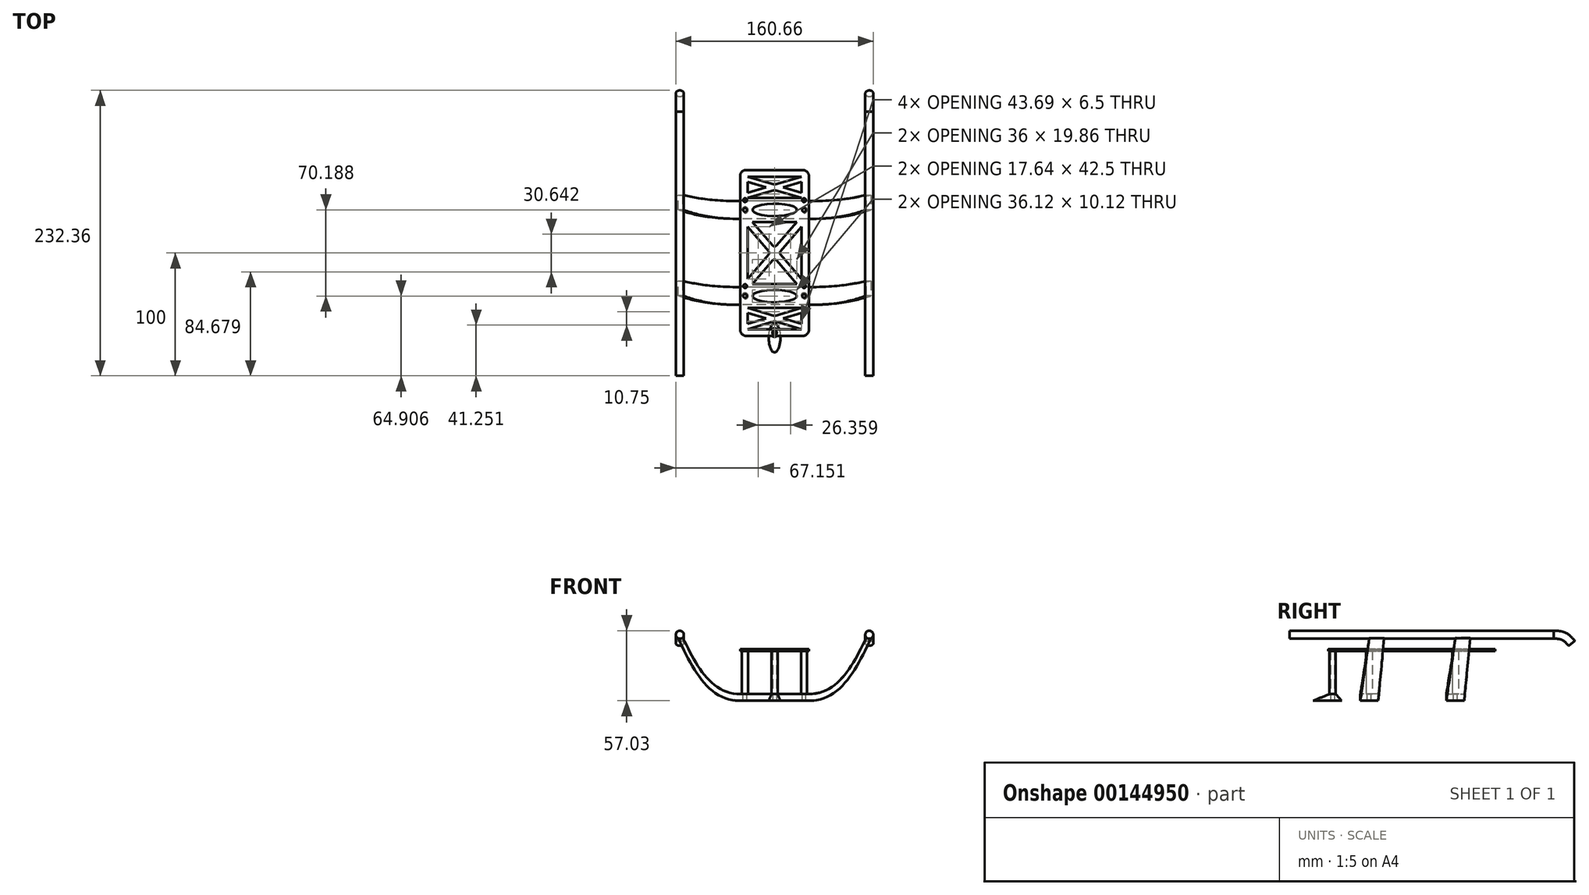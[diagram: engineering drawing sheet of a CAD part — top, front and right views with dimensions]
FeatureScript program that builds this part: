
annotation { "Feature Type Name" : "Feature", "Feature Type Description" : "" }
export const myFeature = defineFeature(function(context is Context, id is Id, definition is map)
    precondition{}
    {
        {
            var Q0;
            Q0=qCreatedBy(makeId("Top.planeOp"),FACE);
            var sketch = newSketch(context, id + "F0", { "sketchPlane" : qUnion([Q0])});
            skCircle(sketch, "E0", {"center": v(24, 35) * mm, "radius": 1.55 * mm});
            skCircle(sketch, "E1.MirrorC", {"center": v(-24, 35) * mm, "radius": 1.55 * mm});
            skCircle(sketch, "E2.MirrorC", {"center": v(-24, -35) * mm, "radius": 1.55 * mm});
            skCircle(sketch, "E3.MirrorC", {"center": v(24, -35) * mm, "radius": 1.55 * mm});
            skLineSegment(sketch, "E4.bottom", {"start": v(27.5, 27.75) * mm, "end": v(-27.5, 27.75) * mm});
            skLineSegment(sketch, "E4.top", {"start": v(27.5, 42.25) * mm, "end": v(-27.5, 42.25) * mm});
            skLineSegment(sketch, "E4.left", {"start": v(27.5, 27.75) * mm, "end": v(27.5, 42.25) * mm});
            skLineSegment(sketch, "E4.right", {"start": v(-27.5, 27.75) * mm, "end": v(-27.5, 42.25) * mm});
            skPoint(sketch, "E4.middle", {"position": v(0, 35) * mm});
            skPoint(sketch, "E5.MirrorP", {"position": v(0, -35) * mm});
            skLineSegment(sketch, "E6.MirrorCS", {"start": v(-27.5, -27.75) * mm, "end": v(-27.5, -42.25) * mm});
            skLineSegment(sketch, "E7.MirrorCS", {"start": v(27.5, -27.75) * mm, "end": v(27.5, -42.25) * mm});
            skLineSegment(sketch, "E8.MirrorCS", {"start": v(27.5, -27.75) * mm, "end": v(-27.5, -27.75) * mm});
            skLineSegment(sketch, "E9.MirrorCS", {"start": v(27.5, -42.25) * mm, "end": v(-27.5, -42.25) * mm});
            skSolve(sketch);
        }
        {
            var Q0;
            Q0 = qSketchRegion(id + "F0", true);
            extrude(context, id + "F1", {"entities" : qUnion([Q0]), "oppositeDirection" : true, "depth" : 5.5 * mm});
        }
        {
            var Q0;
            Q0=makeQuery(id+"F1.opExtrude","CAP_FACE",FACE,{"disambiguationData":[OSD([sQuery(id+"F0.wireOp",EDGE,"E0"),sQuery(id+"F0.wireOp",EDGE,"E1.MirrorC"),sQuery(id+"F0.wireOp",EDGE,"E4.bottom"),sQuery(id+"F0.wireOp",EDGE,"E4.top"),sQuery(id+"F0.wireOp",EDGE,"E4.left"),sQuery(id+"F0.wireOp",EDGE,"E4.right")])],"isStart":true});
            cPlane(context, id + "F2", {"entities" : qUnion([Q0]), "cplaneType" : CPlaneType.OFFSET, "offset" : 47 * mm, "width" : 150 * mm, "height" : 150 * mm});
        }
        {
            var Q0;
            Q0=qCreatedBy(id+"F2.planeOp",FACE);
            var sketch = newSketch(context, id + "F3", { "sketchPlane" : qUnion([Q0])});
            skLineSegment(sketch, "E10.bottom", {"start": v(-79, 47.25) * mm, "end": v(-75, 47.25) * mm});
            skLineSegment(sketch, "E10.top", {"start": v(-79, 35.25) * mm, "end": v(-75, 35.25) * mm});
            skLineSegment(sketch, "E10.left", {"start": v(-79, 47.25) * mm, "end": v(-79, 35.25) * mm});
            skLineSegment(sketch, "E10.right", {"start": v(-75, 47.25) * mm, "end": v(-75, 35.25) * mm});
            skLineSegment(sketch, "E11.bottom", {"start": v(-79, -22.75) * mm, "end": v(-75, -22.75) * mm});
            skLineSegment(sketch, "E11.top", {"start": v(-79, -34.75) * mm, "end": v(-75, -34.75) * mm});
            skLineSegment(sketch, "E11.left", {"start": v(-79, -22.75) * mm, "end": v(-79, -34.75) * mm});
            skLineSegment(sketch, "E11.right", {"start": v(-75, -22.75) * mm, "end": v(-75, -34.75) * mm});
            skLineSegment(sketch, "E12.MirrorCS", {"start": v(79, 47.25) * mm, "end": v(75, 47.25) * mm});
            skLineSegment(sketch, "E13.MirrorCS", {"start": v(79, 35.25) * mm, "end": v(75, 35.25) * mm});
            skLineSegment(sketch, "E14.MirrorCS", {"start": v(79, 47.25) * mm, "end": v(79, 35.25) * mm});
            skLineSegment(sketch, "E15.MirrorCS", {"start": v(75, 47.25) * mm, "end": v(75, 35.25) * mm});
            skLineSegment(sketch, "E16.MirrorCS", {"start": v(79, -22.75) * mm, "end": v(75, -22.75) * mm});
            skLineSegment(sketch, "E17.MirrorCS", {"start": v(79, -34.75) * mm, "end": v(75, -34.75) * mm});
            skLineSegment(sketch, "E18.MirrorCS", {"start": v(75, -22.75) * mm, "end": v(75, -34.75) * mm});
            skLineSegment(sketch, "E19.MirrorCS", {"start": v(79, -22.75) * mm, "end": v(79, -34.75) * mm});
            skSolve(sketch);
        }
        {
            var Q0;
            Q0 = qSketchRegion(id + "F3", true);
            extrude(context, id + "F4", {"entities" : qUnion([Q0]), "depth" : 1 * mm, "symmetric" : true});
        }
        {
            var Q0;
            Q0=makeQuery(id+"F1.opExtrude","SWEPT_FACE",FACE,{"disambiguationData":[OSD([sQuery(id+"F0.wireOp",EDGE,"E4.right")])]});
            var Q1;
            Q1=makeQuery(id+"F4.opExtrude","CAP_FACE",FACE,{"disambiguationData":[OSD([sQuery(id+"F3.wireOp",EDGE,"E10.bottom"),sQuery(id+"F3.wireOp",EDGE,"E10.top"),sQuery(id+"F3.wireOp",EDGE,"E10.left"),sQuery(id+"F3.wireOp",EDGE,"E10.right")])],"isStart":true});
            loft(context, id + "F5", {"operationType" : NewBodyOperationType.ADD, "startCondition" : LoftEndDerivativeType.NORMAL_TO_PROFILE, "startMagnitude" : 1.5, "sheetProfilesArray" : [{ "sheetProfileEntities" : qUnion([Q0]) }, { "sheetProfileEntities" : qUnion([Q1]) }]});
        }
        {
            var Q0;
            Q0=makeQuery(id+"F1.opExtrude","SWEPT_FACE",FACE,{"disambiguationData":[OSD([sQuery(id+"F0.wireOp",EDGE,"E6.MirrorCS")])]});
            var Q1;
            Q1=makeQuery(id+"F4.opExtrude","CAP_FACE",FACE,{"disambiguationData":[OSD([sQuery(id+"F3.wireOp",EDGE,"E11.bottom"),sQuery(id+"F3.wireOp",EDGE,"E11.top"),sQuery(id+"F3.wireOp",EDGE,"E11.left"),sQuery(id+"F3.wireOp",EDGE,"E11.right")])],"isStart":true});
            loft(context, id + "F6", {"operationType" : NewBodyOperationType.ADD, "startCondition" : LoftEndDerivativeType.NORMAL_TO_PROFILE, "startMagnitude" : 1.5, "sheetProfilesArray" : [{ "sheetProfileEntities" : qUnion([Q0]) }, { "sheetProfileEntities" : qUnion([Q1]) }]});
        }
        {
            var Q0;
            Q0=makeQuery(id+"F1.opExtrude","SWEPT_FACE",FACE,{"disambiguationData":[OSD([sQuery(id+"F0.wireOp",EDGE,"E7.MirrorCS")])]});
            var Q1;
            Q1=makeQuery(id+"F4.opExtrude","CAP_FACE",FACE,{"disambiguationData":[OSD([sQuery(id+"F3.wireOp",EDGE,"E16.MirrorCS"),sQuery(id+"F3.wireOp",EDGE,"E17.MirrorCS"),sQuery(id+"F3.wireOp",EDGE,"E18.MirrorCS"),sQuery(id+"F3.wireOp",EDGE,"E19.MirrorCS")])],"isStart":true});
            loft(context, id + "F7", {"operationType" : NewBodyOperationType.ADD, "startCondition" : LoftEndDerivativeType.NORMAL_TO_PROFILE, "startMagnitude" : 1.5, "sheetProfilesArray" : [{ "sheetProfileEntities" : qUnion([Q0]) }, { "sheetProfileEntities" : qUnion([Q1]) }]});
        }
        {
            var Q0;
            Q0=makeQuery(id+"F1.opExtrude","SWEPT_FACE",FACE,{"disambiguationData":[OSD([sQuery(id+"F0.wireOp",EDGE,"E4.left")])]});
            var Q1;
            Q1=makeQuery(id+"F4.opExtrude","CAP_FACE",FACE,{"disambiguationData":[OSD([sQuery(id+"F3.wireOp",EDGE,"E12.MirrorCS"),sQuery(id+"F3.wireOp",EDGE,"E13.MirrorCS"),sQuery(id+"F3.wireOp",EDGE,"E14.MirrorCS"),sQuery(id+"F3.wireOp",EDGE,"E15.MirrorCS")])],"isStart":true});
            loft(context, id + "F8", {"operationType" : NewBodyOperationType.ADD, "startCondition" : LoftEndDerivativeType.NORMAL_TO_PROFILE, "startMagnitude" : 1.5, "sheetProfilesArray" : [{ "sheetProfileEntities" : qUnion([Q0]) }, { "sheetProfileEntities" : qUnion([Q1]) }]});
        }
        {
            var Q0;
            Q0=qCreatedBy(makeId("Front.planeOp"),FACE);
            var sketch = newSketch(context, id + "F9", { "sketchPlane" : qUnion([Q0])});
            skCircle(sketch, "E20", {"center": v(-77.08, 48.25) * mm, "radius": 3.25 * mm});
            skCircle(sketch, "E21.MirrorC", {"center": v(77.08, 48.25) * mm, "radius": 3.25 * mm});
            skSolve(sketch);
        }
        {
            var Q0;
            Q0 = qSketchRegion(id + "F9", true);
            extrude(context, id + "F10", {"entities" : qUnion([Q0]), "operationType" : NewBodyOperationType.ADD, "depth" : 100 * mm, "hasSecondDirection" : true, "secondDirectionOppositeDirection" : true, "secondDirectionDepth" : 115 * mm});
        }
        {
            var Q0;
            Q0=qCreatedBy(makeId("Right.planeOp"),FACE);
            var sketch = newSketch(context, id + "F11", { "sketchPlane" : qUnion([Q0])});
            skFitSpline(sketch, "E22", {"points": [v(115, 54.9) * mm, v(123.56, 53.94) * mm, v(128.8, 51.44) * mm, v(135, 45.49) * mm], "startDerivative": vector(20.16, 0.9) * mm, "endDerivative": vector(29.36, -33.3) * mm});
            skPoint(sketch, "E23", {"position": v(115, 57.99) * mm});
            skSolve(sketch);
        }
        {
            var Q0;
            Q0=makeQuery(id+"F10.opExtrude","CAP_FACE",FACE,{"disambiguationData":[OSD([sQuery(id+"F9.wireOp",EDGE,"E20")])],"isStart":true});
            var Q1;
            Q1=makeQuery(id+"F10.opExtrude","CAP_FACE",FACE,{"disambiguationData":[OSD([sQuery(id+"F9.wireOp",EDGE,"E21.MirrorC")])],"isStart":true});
            var Q2;
            Q2=sQuery(id+"F11.wireOp",EDGE,"E22");
            sweep(context, id + "F12", {"operationType" : NewBodyOperationType.ADD, "profiles" : qUnion([Q0, Q1]), "path" : qUnion([Q2])});
        }
        {
            var Q0;
            Q0=makeQuery(id+"F1.opExtrude","CAP_FACE",FACE,{"disambiguationData":[OSD([sQuery(id+"F0.wireOp",EDGE,"E0"),sQuery(id+"F0.wireOp",EDGE,"E1.MirrorC"),sQuery(id+"F0.wireOp",EDGE,"E4.bottom"),sQuery(id+"F0.wireOp",EDGE,"E4.top"),sQuery(id+"F0.wireOp",EDGE,"E4.left"),sQuery(id+"F0.wireOp",EDGE,"E4.right")])],"isStart":true});
            cPlane(context, id + "F13", {"entities" : qUnion([Q0]), "cplaneType" : CPlaneType.OFFSET, "offset" : 35 * mm, "width" : 150 * mm, "height" : 150 * mm});
        }
        {
            var Q0;
            Q0=qCreatedBy(id+"F13.planeOp",FACE);
            var sketch = newSketch(context, id + "F14", { "sketchPlane" : qUnion([Q0])});
            skLineSegment(sketch, "E24.bottom", {"start": v(23, -67.5) * mm, "end": v(2.55, -67.5) * mm});
            skLineSegment(sketch, "E24.top", {"start": v(23, 67.5) * mm, "end": v(-23, 67.5) * mm});
            skLineSegment(sketch, "E24.left", {"start": v(28, -62.5) * mm, "end": v(28, 62.5) * mm});
            skLineSegment(sketch, "E24.right", {"start": v(-28, -62.5) * mm, "end": v(-28, 62.5) * mm});
            skLineSegment(sketch, "E25", {"start": v(21.85, -57.83) * mm, "end": v(21.85, -48.92) * mm});
            skLineSegment(sketch, "E26", {"start": v(21.85, -48.92) * mm, "end": v(6.88, -53.37) * mm});
            skLineSegment(sketch, "E27", {"start": v(6.88, -53.37) * mm, "end": v(21.85, -57.83) * mm});
            skLineSegment(sketch, "E28.MirrorCS", {"start": v(-6.88, -53.37) * mm, "end": v(-21.85, -57.83) * mm});
            skLineSegment(sketch, "E29.MirrorCS", {"start": v(-21.85, -57.83) * mm, "end": v(-21.85, -48.92) * mm});
            skLineSegment(sketch, "E30.MirrorCS", {"start": v(-21.85, -48.92) * mm, "end": v(-6.88, -53.37) * mm});
            skLineSegment(sketch, "E31", {"start": v(21.85, -62) * mm, "end": v(2.42, -62) * mm});
            skLineSegment(sketch, "E32", {"start": v(-21.85, -62) * mm, "end": v(0, -55.5) * mm});
            skLineSegment(sketch, "E33", {"start": v(0, -55.5) * mm, "end": v(21.85, -62) * mm});
            skLineSegment(sketch, "E34", {"start": v(2.98, -53.37) * mm, "end": v(-2.47, -53.37) * mm});
            skLineSegment(sketch, "E35.MirrorCS", {"start": v(0, -51.25) * mm, "end": v(21.85, -44.75) * mm});
            skLineSegment(sketch, "E36.MirrorCS", {"start": v(21.85, -44.75) * mm, "end": v(-21.85, -44.75) * mm});
            skLineSegment(sketch, "E37.MirrorCS", {"start": v(-21.85, -44.75) * mm, "end": v(0, -51.25) * mm});
            skLineSegment(sketch, "E38.MirrorCS", {"start": v(2.98, 53.37) * mm, "end": v(-2.47, 53.37) * mm});
            skLineSegment(sketch, "E39.MirrorCS", {"start": v(-21.85, 62) * mm, "end": v(0, 55.5) * mm});
            skLineSegment(sketch, "E40.MirrorCS", {"start": v(0, 55.5) * mm, "end": v(21.85, 62) * mm});
            skLineSegment(sketch, "E41.MirrorCS", {"start": v(6.88, 53.37) * mm, "end": v(21.85, 57.83) * mm});
            skLineSegment(sketch, "E42.MirrorCS", {"start": v(21.85, 57.83) * mm, "end": v(21.85, 48.92) * mm});
            skLineSegment(sketch, "E43.MirrorCS", {"start": v(21.85, 48.92) * mm, "end": v(6.88, 53.37) * mm});
            skLineSegment(sketch, "E44.MirrorCS", {"start": v(-21.85, 44.75) * mm, "end": v(0, 51.25) * mm});
            skLineSegment(sketch, "E45.MirrorCS", {"start": v(21.85, 62) * mm, "end": v(-21.85, 62) * mm});
            skLineSegment(sketch, "E46.MirrorCS", {"start": v(-21.85, 48.92) * mm, "end": v(-6.88, 53.37) * mm});
            skLineSegment(sketch, "E47.MirrorCS", {"start": v(-21.85, 57.83) * mm, "end": v(-21.85, 48.92) * mm});
            skLineSegment(sketch, "E48.MirrorCS", {"start": v(-6.88, 53.37) * mm, "end": v(-21.85, 57.83) * mm});
            skLineSegment(sketch, "E49.MirrorCS", {"start": v(21.85, 44.75) * mm, "end": v(-21.85, 44.75) * mm});
            skLineSegment(sketch, "E50.MirrorCS", {"start": v(0, 51.25) * mm, "end": v(21.85, 44.75) * mm});
            skEllipse(sketch, "E51", {"center": v(0, 35.1) * mm, "majorRadius": 18.06 * mm, "minorRadius": 5.06 * mm, "majorAxis": v(1, 0)});
            skEllipse(sketch, "E52.MirrorC", {"center": v(0, -35.1) * mm, "majorRadius": 18.06 * mm, "minorRadius": 5.06 * mm, "majorAxis": v(1, 0)});
            skPoint(sketch, "E53.visualSharp", {"position": v(-28, 67.5) * mm});
            skArc(sketch, "E53.filletArc", {"start": v(-23, 67.5) * mm, "mid": v(-26.54, 66.04) * mm, "end": v(-28, 62.5) * mm});
            skPoint(sketch, "E54.visualSharp", {"position": v(28, 67.5) * mm});
            skArc(sketch, "E54.filletArc", {"start": v(28, 62.5) * mm, "mid": v(26.54, 66.04) * mm, "end": v(23, 67.5) * mm});
            skPoint(sketch, "E55.visualSharp", {"position": v(28, -67.5) * mm});
            skArc(sketch, "E55.filletArc", {"start": v(23, -67.5) * mm, "mid": v(26.54, -66.04) * mm, "end": v(28, -62.5) * mm});
            skPoint(sketch, "E56.visualSharp", {"position": v(-28, -67.5) * mm});
            skArc(sketch, "E56.filletArc", {"start": v(-28, -62.5) * mm, "mid": v(-26.54, -66.04) * mm, "end": v(-23, -67.5) * mm});
            skArc(sketch, "E57", {"start": v(-1.98, -67.68) * mm, "mid": v(0, -68.3) * mm, "end": v(1.98, -67.68) * mm});
            skArc(sketch, "E58.trimOffspring", {"start": v(1.88, -61.84) * mm, "mid": v(0, -61.3) * mm, "end": v(-1.88, -61.84) * mm});
            skLineSegment(sketch, "E59.trimOffspring", {"start": v(-2.42, -62) * mm, "end": v(-21.85, -62) * mm});
            skLineSegment(sketch, "E60.trimOffspring", {"start": v(-2.55, -67.5) * mm, "end": v(-23, -67.5) * mm});
            skPoint(sketch, "E61.visualSharp", {"position": v(2.22, -67.5) * mm});
            skArc(sketch, "E61.filletArc", {"start": v(2.55, -67.5) * mm, "mid": v(2.25, -67.55) * mm, "end": v(1.98, -67.68) * mm});
            skPoint(sketch, "E62.visualSharp", {"position": v(2.1, -62) * mm});
            skArc(sketch, "E62.filletArc", {"start": v(1.88, -61.84) * mm, "mid": v(2.14, -61.96) * mm, "end": v(2.42, -62) * mm});
            skPoint(sketch, "E63.visualSharp", {"position": v(-2.1, -62) * mm});
            skArc(sketch, "E63.filletArc", {"start": v(-2.42, -62) * mm, "mid": v(-2.14, -61.96) * mm, "end": v(-1.88, -61.84) * mm});
            skPoint(sketch, "E64.visualSharp", {"position": v(-2.22, -67.5) * mm});
            skArc(sketch, "E64.filletArc", {"start": v(-1.98, -67.68) * mm, "mid": v(-2.25, -67.55) * mm, "end": v(-2.55, -67.5) * mm});
            skLineSegment(sketch, "E65.bottom", {"start": v(-18, 25.25) * mm, "end": v(18, 25.25) * mm});
            skLineSegment(sketch, "E65.top", {"start": v(-18, -25.25) * mm, "end": v(18, -25.25) * mm});
            skLineSegment(sketch, "E65.left", {"start": v(-22, 21.25) * mm, "end": v(-22, -21.25) * mm});
            skLineSegment(sketch, "E65.right", {"start": v(22, 21.25) * mm, "end": v(22, -21.25) * mm});
            skLineSegment(sketch, "E66", {"start": v(-18, 25.25) * mm, "end": v(-1.52, 6.09) * mm});
            skLineSegment(sketch, "E67", {"start": v(-22, 21.25) * mm, "end": v(-4.84, 1.3) * mm});
            skLineSegment(sketch, "E68", {"start": v(-22, -21.25) * mm, "end": v(-4.84, -1.3) * mm});
            skLineSegment(sketch, "E69", {"start": v(-18, -25.25) * mm, "end": v(-1.52, -6.09) * mm});
            skPoint(sketch, "E70.orphan", {"position": v(-22, 25.25) * mm});
            skPoint(sketch, "E71.orphan", {"position": v(22, 25.25) * mm});
            skPoint(sketch, "E72.orphan", {"position": v(22, -25.25) * mm});
            skPoint(sketch, "E73.orphan", {"position": v(-22, -25.25) * mm});
            skLineSegment(sketch, "E74.trimOffspring", {"start": v(1.52, -6.09) * mm, "end": v(18, -25.25) * mm});
            skLineSegment(sketch, "E75.trimOffspring", {"start": v(1.52, 6.09) * mm, "end": v(18, 25.25) * mm});
            skLineSegment(sketch, "E76.trimOffspring", {"start": v(4.84, -1.3) * mm, "end": v(22, -21.25) * mm});
            skLineSegment(sketch, "E77.trimOffspring", {"start": v(4.84, 1.3) * mm, "end": v(22, 21.25) * mm});
            skPoint(sketch, "E78.visualSharp", {"position": v(0, 4.33) * mm});
            skArc(sketch, "E78.filletArc", {"start": v(-1.52, 6.09) * mm, "mid": v(0, 5.4) * mm, "end": v(1.52, 6.09) * mm});
            skPoint(sketch, "E79.visualSharp", {"position": v(3.72, 0) * mm});
            skArc(sketch, "E79.filletArc", {"start": v(4.84, 1.3) * mm, "mid": v(4.36, 0) * mm, "end": v(4.84, -1.3) * mm});
            skPoint(sketch, "E80.visualSharp", {"position": v(0, -4.33) * mm});
            skArc(sketch, "E80.filletArc", {"start": v(1.52, -6.09) * mm, "mid": v(0, -5.4) * mm, "end": v(-1.52, -6.09) * mm});
            skPoint(sketch, "E81.visualSharp", {"position": v(-3.72, 0) * mm});
            skArc(sketch, "E81.filletArc", {"start": v(-4.84, -1.3) * mm, "mid": v(-4.36, 0) * mm, "end": v(-4.84, 1.3) * mm});
            skSolve(sketch);
        }
        {
            var Q0;
            Q0 = qSketchRegion(id + "F14", true);
            extrude(context, id + "F15", {"entities" : qUnion([Q0]), "depth" : 1.5 * mm});
        }
        {
            var Q0;
            Q0=makeQuery(id+"F0.imprint","IMPRINT",FACE,{"disambiguationData":[TD([[makeQuery(id+"F0.imprint","IMPRINT",EDGE,{"derivedFrom":sQuery(id+"F0.wireOp",EDGE,"E3.MirrorC")}),1.0]])]});
            var sketch = newSketch(context, id + "F16", { "sketchPlane" : qUnion([Q0])});
            skEllipse(sketch, "E82", {"center": v(0, -64.7) * mm, "majorRadius": 2.5 * mm, "minorRadius": 2.5 * mm, "majorAxis": v(0, 1)});
            skSolve(sketch);
        }
        {
            var Q0;
            Q0=makeQuery(id+"F1.opExtrude","CAP_FACE",FACE,{"disambiguationData":[OSD([sQuery(id+"F0.wireOp",EDGE,"E3.MirrorC"),sQuery(id+"F0.wireOp",EDGE,"E2.MirrorC"),sQuery(id+"F0.wireOp",EDGE,"E6.MirrorCS"),sQuery(id+"F0.wireOp",EDGE,"E7.MirrorCS"),sQuery(id+"F0.wireOp",EDGE,"E8.MirrorCS"),sQuery(id+"F0.wireOp",EDGE,"E9.MirrorCS")])],"isStart":false});
            var sketch = newSketch(context, id + "F17", { "sketchPlane" : qUnion([Q0])});
            skEllipse(sketch, "E83", {"center": v(0, 69.16) * mm, "majorRadius": 11.75 * mm, "minorRadius": 4.76 * mm, "majorAxis": v(0, -1)});
            skSolve(sketch);
        }
        {
            var Q1;
            Q1 = qSketchRegion(id + "F16", true);
            var Q2;
            Q2 = qSketchRegion(id + "F17", true);
            loft(context, id + "F18", {"sheetProfilesArray" : [{ "sheetProfileEntities" : qUnion([Q1]) }, { "sheetProfileEntities" : qUnion([Q2]) }]});
        }
        {
            var Q0;
            Q0=makeQuery(id+"F15.opExtrude","CAP_FACE",FACE,{"disambiguationData":[OSD([sQuery(id+"F14.wireOp",EDGE,"E24.bottom"),sQuery(id+"F14.wireOp",EDGE,"E24.top"),sQuery(id+"F14.wireOp",EDGE,"E24.left"),sQuery(id+"F14.wireOp",EDGE,"E24.right"),sQuery(id+"F14.wireOp",EDGE,"E25"),sQuery(id+"F14.wireOp",EDGE,"E26"),sQuery(id+"F14.wireOp",EDGE,"E27"),sQuery(id+"F14.wireOp",EDGE,"E28.MirrorCS"),sQuery(id+"F14.wireOp",EDGE,"E29.MirrorCS"),sQuery(id+"F14.wireOp",EDGE,"E30.MirrorCS"),sQuery(id+"F14.wireOp",EDGE,"E31"),sQuery(id+"F14.wireOp",EDGE,"E32"),sQuery(id+"F14.wireOp",EDGE,"E33"),sQuery(id+"F14.wireOp",EDGE,"E35.MirrorCS"),sQuery(id+"F14.wireOp",EDGE,"E36.MirrorCS"),sQuery(id+"F14.wireOp",EDGE,"E37.MirrorCS"),sQuery(id+"F14.wireOp",EDGE,"E39.MirrorCS"),sQuery(id+"F14.wireOp",EDGE,"E40.MirrorCS"),sQuery(id+"F14.wireOp",EDGE,"E41.MirrorCS"),sQuery(id+"F14.wireOp",EDGE,"E42.MirrorCS"),sQuery(id+"F14.wireOp",EDGE,"E43.MirrorCS"),sQuery(id+"F14.wireOp",EDGE,"E44.MirrorCS"),sQuery(id+"F14.wireOp",EDGE,"E45.MirrorCS"),sQuery(id+"F14.wireOp",EDGE,"E46.MirrorCS"),sQuery(id+"F14.wireOp",EDGE,"E47.MirrorCS"),sQuery(id+"F14.wireOp",EDGE,"E48.MirrorCS"),sQuery(id+"F14.wireOp",EDGE,"E49.MirrorCS"),sQuery(id+"F14.wireOp",EDGE,"E50.MirrorCS"),sQuery(id+"F14.wireOp",EDGE,"41cgnIPL-npWc-O3OT-IIvp-3opdmebJhPuE"),sQuery(id+"F14.wireOp",EDGE,"cnqzEcAR-puum-2v5H-bPeM-nhvkTepjbg7f"),sQuery(id+"F14.wireOp",EDGE,"ZUyBv95D-Vip0-E0xQ-HOKZ-qXVskTSMhhZ4"),sQuery(id+"F14.wireOp",EDGE,"QW4Knzpe-XfPx-6G3O-fQ7r-xCA8DHTI8llc"),sQuery(id+"F14.wireOp",EDGE,"u5ZCEIEt-8dGf-CeKo-rW56-BvbBlPJxl9Av"),sQuery(id+"F14.wireOp",EDGE,"tRerhao7-xNC6-3Qj8-PqBg-vBzmJME0fykC"),sQuery(id+"F14.wireOp",EDGE,"34f72953-b367-436d-b2e1-794d6ac8d1dc0.MirrorCS"),sQuery(id+"F14.wireOp",EDGE,"e1a0620d-9711-44c7-a052-cdfd6f5fabb40.MirrorCS"),sQuery(id+"F14.wireOp",EDGE,"f9968c47-6fa3-4d05-afce-87440d7f02980.MirrorCS"),sQuery(id+"F14.wireOp",EDGE,"cde4a5db-1fe4-4333-8411-bf7d7e01e0120.MirrorCS"),sQuery(id+"F14.wireOp",EDGE,"0ad4e2a6-e274-4dd3-8f10-cc4f6a0458050.MirrorCS"),sQuery(id+"F14.wireOp",EDGE,"46e521f6-c0f6-47cd-9bc7-52dcf3b3e5ab0.MirrorCS"),sQuery(id+"F14.wireOp",EDGE,"E51"),sQuery(id+"F14.wireOp",EDGE,"E52.MirrorC"),sQuery(id+"F14.wireOp",EDGE,"E53.filletArc"),sQuery(id+"F14.wireOp",EDGE,"E54.filletArc"),sQuery(id+"F14.wireOp",EDGE,"E55.filletArc"),sQuery(id+"F14.wireOp",EDGE,"E56.filletArc")])],"isStart":true});
            var sketch = newSketch(context, id + "F19", { "sketchPlane" : qUnion([Q0])});
            skCircle(sketch, "E84", {"center": v(0, 64.95) * mm, "radius": 2.5 * mm});
            skSolve(sketch);
        }
        {
            var Q0;
            Q0 = qSketchRegion(id + "F19", true);
            var Q1;
            Q1=makeQuery(id+"F18.opLoft","CAP_FACE",FACE,{"disambiguationData":[OSD([makeQuery(id+"F16.imprint","IMPRINT",FACE,{"disambiguationData":[TD([[makeQuery(id+"F16.imprint","IMPRINT",EDGE,{"derivedFrom":sQuery(id+"F16.wireOp",EDGE,"E82")}),1.0]])]})])],"isStart":true});
            extrude(context, id + "F20", {"entities" : qUnion([Q0]), "endBound" : BoundingType.UP_TO_SURFACE, "endBoundEntityFace" : qUnion([Q1]), "depth" : 25 * mm});
        }
        {
            var Q0;
            Q0=makeQuery(id+"F18.opLoft","CAP_FACE",FACE,{"disambiguationData":[OSD([makeQuery(id+"F17.imprint","IMPRINT",FACE,{"disambiguationData":[TD([[makeQuery(id+"F17.imprint","IMPRINT",EDGE,{"derivedFrom":sQuery(id+"F17.wireOp",EDGE,"E83")}),1.0]])]})])],"isStart":true});
            var sketch = newSketch(context, id + "F21", { "sketchPlane" : qUnion([Q0])});
            skCircle(sketch, "E85", {"center": v(0, 64.95) * mm, "radius": 1.65 * mm});
            skSolve(sketch);
        }
        {
            var Q0;
            Q0 = qSketchRegion(id + "F21", true);
            extrude(context, id + "F22", {"entities" : qUnion([Q0]), "operationType" : NewBodyOperationType.REMOVE, "endBound" : BoundingType.THROUGH_ALL, "oppositeDirection" : true, "depth" : 25 * mm});
        }
        {
            var Q0;
            Q0=makeQuery(id+"F15.opExtrude","CAP_FACE",FACE,{"disambiguationData":[OSD([sQuery(id+"F14.wireOp",EDGE,"E24.bottom"),sQuery(id+"F14.wireOp",EDGE,"E24.top"),sQuery(id+"F14.wireOp",EDGE,"E24.left"),sQuery(id+"F14.wireOp",EDGE,"E24.right")])],"isStart":false});
            var sketch = newSketch(context, id + "F23", { "sketchPlane" : qUnion([Q0])});
            skCircle(sketch, "E86", {"center": v(-24, 35) * mm, "radius": 1.55 * mm});
            skCircle(sketch, "E87", {"center": v(24, 35) * mm, "radius": 1.55 * mm});
            skCircle(sketch, "E88", {"center": v(-24, -35) * mm, "radius": 1.55 * mm});
            skCircle(sketch, "E89", {"center": v(24, -35) * mm, "radius": 1.55 * mm});
            skCircle(sketch, "E90", {"center": v(-24, -27) * mm, "radius": 1.55 * mm});
            skCircle(sketch, "E91", {"center": v(-24, 43) * mm, "radius": 1.55 * mm});
            skCircle(sketch, "E92.MirrorC", {"center": v(24, 43) * mm, "radius": 1.55 * mm});
            skCircle(sketch, "E93.MirrorC", {"center": v(24, -27) * mm, "radius": 1.55 * mm});
            skSolve(sketch);
        }
        {
            var Q0;
            Q0 = qSketchRegion(id + "F23", true);
            var Q1;
            Q1=makeQuery(id+"F15.opExtrude","CAP_FACE",FACE,{"disambiguationData":[OSD([sQuery(id+"F14.wireOp",EDGE,"E24.bottom"),sQuery(id+"F14.wireOp",EDGE,"E24.top"),sQuery(id+"F14.wireOp",EDGE,"E24.left"),sQuery(id+"F14.wireOp",EDGE,"E24.right")])],"isStart":true});
            extrude(context, id + "F24", {"entities" : qUnion([Q0]), "operationType" : NewBodyOperationType.REMOVE, "endBound" : BoundingType.UP_TO_SURFACE, "oppositeDirection" : true, "endBoundEntityFace" : qUnion([Q1]), "depth" : 25 * mm});
        }
        {
            var Q0;
            Q0=makeQuery(id+"F0.imprint","IMPRINT",FACE,{"disambiguationData":[TD([[makeQuery(id+"F0.imprint","IMPRINT",EDGE,{"derivedFrom":sQuery(id+"F0.wireOp",EDGE,"E0")}),-1.0]])]});
            var sketch = newSketch(context, id + "F25", { "sketchPlane" : qUnion([Q0])});
            skCircle(sketch, "E94", {"center": v(-24, 35) * mm, "radius": 2.5 * mm});
            skCircle(sketch, "E95", {"center": v(24, 35) * mm, "radius": 2.5 * mm});
            skCircle(sketch, "E96", {"center": v(-24, -35) * mm, "radius": 2.5 * mm});
            skCircle(sketch, "E97", {"center": v(24, -35) * mm, "radius": 2.5 * mm});
            skSolve(sketch);
        }
        {
            var Q0;
            Q0 = qSketchRegion(id + "F25", true);
            var Q1;
            Q1=makeQuery(id+"F15.opExtrude","CAP_FACE",FACE,{"disambiguationData":[OSD([sQuery(id+"F14.wireOp",EDGE,"E24.bottom"),sQuery(id+"F14.wireOp",EDGE,"E24.top"),sQuery(id+"F14.wireOp",EDGE,"E24.left"),sQuery(id+"F14.wireOp",EDGE,"E24.right")])],"isStart":true});
            extrude(context, id + "F26", {"entities" : qUnion([Q0]), "endBound" : BoundingType.UP_TO_SURFACE, "endBoundEntityFace" : qUnion([Q1]), "depth" : 25 * mm});
        }
    });
